# Revit family: KEUCO_34915011911
name_source: partatom
category: Allgemeines Modell
revit_build: Autodesk Revit 2016 (Build: 20150220_1215(x64)
units: mm (PartAtom-declared; Revit-internal decimal feet)

## family parameters
Arbeitsebenenbasiert = Ja
Beim Laden mit Abzugskörper schneiden = Nein
Bemaßung runder Anschluss = Durchmesser verwenden
Gemeinsam genutzt = Nein
Immer vertikal = Nein
Kann Basisbauteil für Bewehrung sein = Nein
Raumberechnungspunkt = Nein
Teiletyp = Normal

## types (12) — shared parameters
Hersteller = KEUCO
Material Stange = 1160 mm  [stored 3.80577 ft]
Serie = Plan
URL = https://www.keuco.com
Verbindung = 80 mm  [stored 0.262467 ft]
Verwendung = CA / DU
Vorgabe-Ansicht = 1219 mm
zero-valued in all types: Gewicht

## per-type parameters (varying)
| type | Ausschreibungstext | Beschreibung | Stange A Länge  | Stange B Länge | Stange Material |
| 34915016611 | KEUCO PLAN CARE Duschhandlauf mit Brausestange 34915016611, 
hochglanzverchromter Duschhandlauf mit Brausestange, 
Winkel/T-Form, komplett mit Brauseschieber,
in ästhetischem, funktionalem und ergonomischem Design,
die Brausestange ist vor der Montage frei positionierbar,
Ausführung rechts und links verwendbar, 
speziell für den Dusch- und Wannenbereich 
als Hilfe zum Festhalten und Abstützen,
bis 115 kg belastbar, antistatisch, leicht zu reinigen,
Außenmaß 797/797/1263 mm
Achsmaß waagerecht 600/600 mm, senkrecht 1100 mm
Rohrdurchmesser 33 mm, 6 Rosetten Durchmesser 82 mm,
Ausladung 90 mm, Wandabstand 57 mm,
der Duschhandlauf wird verdeckt angebracht

Im Lieferumfang enthalten: 
6 x Befestigungs-Set 
1 Art.-Nr. 34990000100 (je 1 x pro Wandbefestigung) 

Der Handlauf ist Bauart geprüft

Der Griff ist kombinierbar mit dem Duschspritzschutz 34940 
und dem Klappsitz mit Rückenlehne 34981

Weitere Befestigungs-Sets
(je nach Ankergrund/Mauerwerk):
6 x Befestigungs-Set 4 (Art.-Nr. 34990000200) oder
6 x Befestigungs-Set 7 (Art.-Nr. 34993000200) | rechts und links verwendbar
komplett mit Brauseschieber
Brausestange vor Montage frei positionierbar | 796 mm  [stored 2.61155 ft] | 720 mm  [stored 2.3622 ft] | Stahl, verchromt |
| 34915016911 | KEUCO PLAN CARE Duschhandlauf mit Brausestange 34915016911 
hochglanzverchromter Duschhandlauf mit Brausestange, 
Winkel/T-Form, komplett mit Brauseschieber,
in ästhetischem, funktionalem und ergonomischem Design,
die Brausestange ist vor der Montage frei positionierbar,
Ausführung rechts und links verwendbar, 
speziell für den Dusch- und Wannenbereich 
als Hilfe zum Festhalten und Abstützen,
bis 115 kg belastbar, antistatisch, leicht zu reinigen,
Außenmaß 797/1097/1263 mm
Achsmaß waagerecht 600/900 mm, senkrecht 1100 mm
Rohrdurchmesser 33 mm, 6 Rosetten Durchmesser 82 mm,
Ausladung 90 mm, Wandabstand 57 mm,
der Duschhandlauf wird verdeckt angebracht

Im Lieferumfang enthalten: 
6 x Befestigungs-Set 
1 Art.-Nr. 34990000100 (je 1 x pro Wandbefestigung) 

Der Handlauf ist Bauart geprüft

Der Griff ist kombinierbar mit dem Duschspritzschutz 34940 
und dem Klappsitz mit Rückenlehne 34981

Weitere Befestigungs-Sets
(je nach Ankergrund/Mauerwerk):
6 x Befestigungs-Set 4 (Art.-Nr. 34990000200) oder
6 x Befestigungs-Set 7 (Art.-Nr. 34993000200) | rechts und links verwendbar
komplett mit Brauseschieber
Brausestange vor Montage frei positionierbar | 796 mm  [stored 2.61155 ft] | 1020 mm  [stored 3.34646 ft] | Stahl, verchromt |
| 34915019611 | KEUCO PLAN CARE Duschhandlauf mit Brausestange 34915019611 
hochglanzverchromter Duschhandlauf mit Brausestange, 
Winkel/T-Form, komplett mit Brauseschieber,
in ästhetischem, funktionalem und ergonomischem Design,
die Brausestange ist vor der Montage frei positionierbar,
Ausführung rechts und links verwendbar, 
speziell für den Dusch- und Wannenbereich 
als Hilfe zum Festhalten und Abstützen,
bis 115 kg belastbar, antistatisch, leicht zu reinigen,
Außenmaß 1097/797/1263 mm
Achsmaß waagerecht 900/600 mm, senkrecht 1100 mm
Rohrdurchmesser 33 mm, 6 Rosetten Durchmesser 82 mm,
Ausladung 90 mm, Wandabstand 57 mm,
der Duschhandlauf wird verdeckt angebracht

Im Lieferumfang enthalten: 
6 x Befestigungs-Set 
1 Art.-Nr. 34990000100 (je 1 x pro Wandbefestigung) 

Der Handlauf ist Bauart geprüft

Der Griff ist kombinierbar mit dem Duschspritzschutz 34940 
und dem Klappsitz mit Rückenlehne 34981

Weitere Befestigungs-Sets
(je nach Ankergrund/Mauerwerk):
6 x Befestigungs-Set 4 (Art.-Nr. 34990000200) oder
6 x Befestigungs-Set 7 (Art.-Nr. 34993000200) | rechts und links verwendbar
komplett mit Brauseschieber
Brausestange vor Montage frei positionierbar | 1096 mm  [stored 3.5958 ft] | 720 mm  [stored 2.3622 ft] | Stahl, verchromt |
| 34915019911 | KEUCO PLAN CARE Duschhandlauf mit Brausestange 34915019911 
hochglanzverchromter Duschhandlauf mit Brausestange, 
Winkel/T-Form, komplett mit Brauseschieber,
in ästhetischem, funktionalem und ergonomischem Design,
die Brausestange ist vor der Montage frei positionierbar,
Ausführung rechts und links verwendbar, 
speziell für den Dusch- und Wannenbereich 
als Hilfe zum Festhalten und Abstützen,
bis 115 kg belastbar, antistatisch, leicht zu reinigen,
Außenmaß 1097/1097/1263 mm
Achsmaß waagerecht 900/900 mm, senkrecht 1100 mm,
Rohrdurchmesser 33 mm, 6 Rosetten Durchmesser 82 mm,
Ausladung 90 mm, Wandabstand 57 mm,
der Duschhandlauf wird verdeckt angebracht

Im Lieferumfang enthalten: 
6 x Befestigungs-Set 
1 Art.-Nr. 34990000100 (je 1 x pro Wandbefestigung) 

Der Handlauf ist Bauart geprüft

Der Griff ist kombinierbar mit dem Duschspritzschutz 34940 
und dem Klappsitz mit Rückenlehne 34981

Weitere Befestigungs-Sets
(je nach Ankergrund/Mauerwerk):
6 x Befestigungs-Set 4 (Art.-Nr. 34990000200) oder
6 x Befestigungs-Set 7 (Art.-Nr. 34993000200) | rechts und links verwendbar
komplett mit Brauseschieber
Brausestange vor Montage frei positionierbar | 1096 mm  [stored 3.5958 ft] | 1020 mm  [stored 3.34646 ft] | Stahl, verchromt |
| 34915019111 | KEUCO PLAN CARE Duschhandlauf mit Brausestange 34915019111 
hochglanzverchromter Duschhandlauf mit Brausestange, 
Winkel/T-Form, komplett mit Brauseschieber,
in ästhetischem, funktionalem und ergonomischem Design,
die Brausestange ist vor der Montage frei positionierbar,
Ausführung rechts und links verwendbar, 
speziell für den Dusch- und Wannenbereich 
als Hilfe zum Festhalten und Abstützen,
bis 115 kg belastbar, antistatisch, leicht zu reinigen,
Außenmaß 1097/1297/1263 mm
Achsmaß waagerecht 900/1100 mm, senkrecht 1100 mm
Rohrdurchmesser 33 mm, 6 Rosetten Durchmesser 82 mm,
Ausladung 90 mm, Wandabstand 57 mm,
der Duschhandlauf wird verdeckt angebracht

Im Lieferumfang enthalten: 
6 x Befestigungs-Set 
1 Art.-Nr. 34990000100 (je 1 x pro Wandbefestigung) 

Der Handlauf ist Bauart geprüft

Der Griff ist kombinierbar mit dem Duschspritzschutz 34940 
und dem Klappsitz mit Rückenlehne 34981

Weitere Befestigungs-Sets
(je nach Ankergrund/Mauerwerk):
6 x Befestigungs-Set 4 (Art.-Nr. 34990000200) oder
6 x Befestigungs-Set 7 (Art.-Nr. 34993000200) | rechts und links verwendbar
komplett mit Brauseschieber
Brausestange vor Montage frei positionierbar | 1096 mm  [stored 3.5958 ft] | 1220 mm  [stored 4.00262 ft] | Stahl, verchromt |
| 34915011911 | KEUCO PLAN CARE Duschhandlauf mit Brausestange 34915011911 
hochglanzverchromter Duschhandlauf mit Brausestange, 
Winkel/T-Form, komplett mit Brauseschieber,
in ästhetischem, funktionalem und ergonomischem Design,
die Brausestange ist vor der Montage frei positionierbar,
Ausführung rechts und links verwendbar, 
speziell für den Dusch- und Wannenbereich 
als Hilfe zum Festhalten und Abstützen,
bis 115 kg belastbar, antistatisch, leicht zu reinigen,
Außenmaß 1297/1097/1263 mm
Achsmaß waagerecht 1100/900 mm, senkrecht 1100 mm
Rohrdurchmesser 33 mm, 6 Rosetten Durchmesser 82 mm,
Ausladung 90 mm, Wandabstand 57 mm,
der Duschhandlauf wird verdeckt angebracht

Im Lieferumfang enthalten: 
6 x Befestigungs-Set 
1 Art.-Nr. 34990000100 (je 1 x pro Wandbefestigung) 

Der Handlauf ist Bauart geprüft

Der Griff ist kombinierbar mit dem Duschspritzschutz 34940 
und dem Klappsitz mit Rückenlehne 34981

Weitere Befestigungs-Sets
(je nach Ankergrund/Mauerwerk):
6 x Befestigungs-Set 4 (Art.-Nr. 34990000200) oder
6 x Befestigungs-Set 7 (Art.-Nr. 34993000200) | komplett mit Brauseschieber
rechts und links verwendbar
Brausestange vor Montage frei positionierbar | 1296 mm  [stored 4.25197 ft] | 1020 mm  [stored 3.34646 ft] | Stahl, verchromt |
| 34915176611 | KEUCO PLAN CARE Duschhandlauf mit Brausestange 34915176611 
Duschhandlauf mit Brausestange, 
Aluminium silber-eloxiert (E6 EV1)/verchromt,
Winkel/T-Form, komplett mit Brauseschieber,
in ästhetischem, funktionalem und ergonomischem Design,
die Brausestange ist vor der Montage frei positionierbar,
Ausführung rechts und links verwendbar, 
speziell für den Dusch- und Wannenbereich 
als Hilfe zum Festhalten und Abstützen,
bis 115 kg belastbar, antistatisch, leicht zu reinigen,
Außenmaß 797/797/1263 mm,
Achsmaß waagerecht 600/600 mm, senkrecht 1100 mm,
Rohrdurchmesser 33 mm, 6 Rosetten Durchmesser 82 mm,
Ausladung 90 mm, Wandabstand 57 mm,
der Duschhandlauf wird verdeckt angebracht

Im Lieferumfang enthalten: 
6 x Befestigungs-Set 
1 Art.-Nr. 34990000100 (je 1 x pro Wandbefestigung) 

Der Handlauf ist Bauart geprüft

Der Griff ist kombinierbar mit dem Duschspritzschutz 34940 
und dem Klappsitz mit Rückenlehne 34981

Weitere Befestigungs-Sets
(je nach Ankergrund/Mauerwerk):
6 x Befestigungs-Set 4 (Art.-Nr. 34990000200) oder
6 x Befestigungs-Set 7 (Art.-Nr. 34993000200) | rechts und links verwendbar
komplett mit Brauseschieber
Brausestange vor Montage frei positionierbar | 796 mm  [stored 2.61155 ft] | 720 mm  [stored 2.3622 ft] | Aluminium 1100-H18 |
| 34915176911 | KEUCO PLAN CARE Duschhandlauf mit Brausestange 34915176911 
Duschhandlauf mit Brausestange, 
Aluminium silber-eloxiert (E6 EV1)/verchromt,
Winkel/T-Form, komplett mit Brauseschieber,
in ästhetischem, funktionalem und ergonomischem Design,
die Brausestange ist vor der Montage frei positionierbar,
Ausführung rechts und links verwendbar, 
speziell für den Dusch- und Wannenbereich 
als Hilfe zum Festhalten und Abstützen,
bis 115 kg belastbar, antistatisch, leicht zu reinigen,
Außenmaß 797/1097/1263 mm,
Achsmaß waagerecht 600/900 mm, senkrecht 1100 mm,
Rohrdurchmesser 33 mm, 6 Rosetten Durchmesser 82 mm,
Ausladung 90 mm, Wandabstand 57 mm,
der Duschhandlauf wird verdeckt angebracht

Im Lieferumfang enthalten: 
6 x Befestigungs-Set 
1 Art.-Nr. 34990000100 (je 1 x pro Wandbefestigung) 

Der Handlauf ist Bauart geprüft

Der Griff ist kombinierbar mit dem Duschspritzschutz 34940 
und dem Klappsitz mit Rückenlehne 34981

Weitere Befestigungs-Sets
(je nach Ankergrund/Mauerwerk):
6 x Befestigungs-Set 4 (Art.-Nr. 34990000200) oder
6 x Befestigungs-Set 7 (Art.-Nr. 34993000200) | rechts und links verwendbar
komplett mit Brauseschieber
Brausestange vor Montage frei positionierbar | 796 mm  [stored 2.61155 ft] | 1020 mm  [stored 3.34646 ft] | Aluminium 1100-H18 |
| 34915179611 | KEUCO PLAN CARE Duschhandlauf mit Brausestange 34915179611 
Duschhandlauf mit Brausestange, 
Aluminium silber-eloxiert (E6 EV1)/verchromt,
Winkel/T-Form, komplett mit Brauseschieber,
in ästhetischem, funktionalem und ergonomischem Design,
die Brausestange ist vor der Montage frei positionierbar,
Ausführung rechts und links verwendbar, 
speziell für den Dusch- und Wannenbereich 
als Hilfe zum Festhalten und Abstützen,
bis 115 kg belastbar, antistatisch, leicht zu reinigen,
Außenmaß 1097/797/1263 mm,
Achsmaß waagerecht 900/600 mm, senkrecht 1100 mm,
Rohrdurchmesser 33 mm, 6 Rosetten Durchmesser 82 mm,
Ausladung 90 mm, Wandabstand 57 mm,
der Duschhandlauf wird verdeckt angebracht

Im Lieferumfang enthalten: 
6 x Befestigungs-Set 
1 Art.-Nr. 34990000100 (je 1 x pro Wandbefestigung) 

Der Handlauf ist Bauart geprüft

Der Griff ist kombinierbar mit dem Duschspritzschutz 34940 
und dem Klappsitz mit Rückenlehne 34981

Weitere Befestigungs-Sets
(je nach Ankergrund/Mauerwerk):
6 x Befestigungs-Set 4 (Art.-Nr. 34990000200) oder
6 x Befestigungs-Set 7 (Art.-Nr. 34993000200) | rechts und links verwendbar
komplett mit Brauseschieber
Brausestange vor Montage frei positionierbar | 1096 mm  [stored 3.5958 ft] | 720 mm  [stored 2.3622 ft] | Aluminium 1100-H18 |
| 34915179911 | KEUCO PLAN CARE Duschhandlauf mit Brausestange 34915179911 
Duschhandlauf mit Brausestange, 
Aluminium silber-eloxiert (E6 EV1)/verchromt,
Winkel/T-Form, komplett mit Brauseschieber,
in ästhetischem, funktionalem und ergonomischem Design,
die Brausestange ist vor der Montage frei positionierbar,
Ausführung rechts und links verwendbar, 
speziell für den Dusch- und Wannenbereich 
als Hilfe zum Festhalten und Abstützen,
bis 115 kg belastbar, antistatisch, leicht zu reinigen,
Außenmaß 1097/1097/1263 mm,
Achsmaß waagerecht 900/900 mm, senkrecht 1100 mm,
Rohrdurchmesser 33 mm, 6 Rosetten Durchmesser 82 mm,
Ausladung 90 mm, Wandabstand 57 mm,
der Duschhandlauf wird verdeckt angebracht

Im Lieferumfang enthalten: 
6 x Befestigungs-Set 
1 Art.-Nr. 34990000100 (je 1 x pro Wandbefestigung) 

Der Handlauf ist Bauart geprüft

Der Griff ist kombinierbar mit dem Duschspritzschutz 34940 
und dem Klappsitz mit Rückenlehne 34981

Weitere Befestigungs-Sets
(je nach Ankergrund/Mauerwerk):
6 x Befestigungs-Set 4 (Art.-Nr. 34990000200) oder
6 x Befestigungs-Set 7 (Art.-Nr. 34993000200) | rechts und links verwendbar
komplett mit Brauseschieber
Brausestange vor Montage frei positionierbar | 1096 mm  [stored 3.5958 ft] | 1020 mm  [stored 3.34646 ft] | Aluminium 1100-H18 |
| 34915179111 | KEUCO PLAN CARE Duschhandlauf mit Brausestange 34915179111 
Duschhandlauf mit Brausestange, 
Aluminium silber-eloxiert (E6 EV1)/verchromt,
Winkel/T-Form, komplett mit Brauseschieber,
in ästhetischem, funktionalem und ergonomischem Design,
die Brausestange ist vor der Montage frei positionierbar,
Ausführung rechts und links verwendbar, 
speziell für den Dusch- und Wannenbereich 
als Hilfe zum Festhalten und Abstützen,
bis 115 kg belastbar, antistatisch, leicht zu reinigen,
Außenmaß 1097/1297/1263 mm,
Achsmaß waagerecht 900/1100 mm, senkrecht 1100 mm,
Rohrdurchmesser 33 mm, 6 Rosetten Durchmesser 82 mm,
Ausladung 90 mm, Wandabstand 57 mm,
der Duschhandlauf wird verdeckt angebracht

Im Lieferumfang enthalten: 
6 x Befestigungs-Set 
1 Art.-Nr. 34990000100 (je 1 x pro Wandbefestigung) 

Der Handlauf ist Bauart geprüft

Der Griff ist kombinierbar mit dem Duschspritzschutz 34940 
und dem Klappsitz mit Rückenlehne 34981

Weitere Befestigungs-Sets
(je nach Ankergrund/Mauerwerk):
6 x Befestigungs-Set 4 (Art.-Nr. 34990000200) oder
6 x Befestigungs-Set 7 (Art.-Nr. 34993000200) | rechts und links verwendbar
komplett mit Brauseschieber
Brausestange vor Montage frei positionierbar | 1096 mm  [stored 3.5958 ft] | 1220 mm  [stored 4.00262 ft] | Aluminium 1100-H18 |
| 34915171911 | KEUCO PLAN CARE Duschhandlauf mit Brausestange 34915171911 
Duschhandlauf mit Brausestange, 
Aluminium silber-eloxiert (E6 EV1)/verchromt,
Winkel/T-Form, komplett mit Brauseschieber,
in ästhetischem, funktionalem und ergonomischem Design,
die Brausestange ist vor der Montage frei positionierbar,
Ausführung rechts und links verwendbar, 
speziell für den Dusch- und Wannenbereich 
als Hilfe zum Festhalten und Abstützen,
bis 115 kg belastbar, antistatisch, leicht zu reinigen,
Außenmaß 1297/1097/1263 mm,
Achsmaß waagerecht 1100/900 mm, senkrecht 1100 mm,
Rohrdurchmesser 33 mm, 6 Rosetten Durchmesser 82 mm,
Ausladung 90 mm, Wandabstand 57 mm,
der Duschhandlauf wird verdeckt angebracht

Im Lieferumfang enthalten: 
6 x Befestigungs-Set 
1 Art.-Nr. 34990000100 (je 1 x pro Wandbefestigung) 

Der Handlauf ist Bauart geprüft

Der Griff ist kombinierbar mit dem Duschspritzschutz 34940 
und dem Klappsitz mit Rückenlehne 34981

Weitere Befestigungs-Sets
(je nach Ankergrund/Mauerwerk):
6 x Befestigungs-Set 4 (Art.-Nr. 34990000200) oder
6 x Befestigungs-Set 7 (Art.-Nr. 34993000200) | rechts und links verwendbar
komplett mit Brauseschieber
Brausestange vor Montage frei positionierbar | 1296 mm  [stored 4.25197 ft] | 1020 mm  [stored 3.34646 ft] | Aluminium 1100-H18 |

note: column(s) folded — value = type name in every type: Artikelnummer

note: [stored X ft] marks values corroborated as IEEE doubles in the binary element streams (Revit-internal decimal feet)

## geometry (parser evidence)
native form markers: Sweep x3
no freeform markers — native parametric forms only
